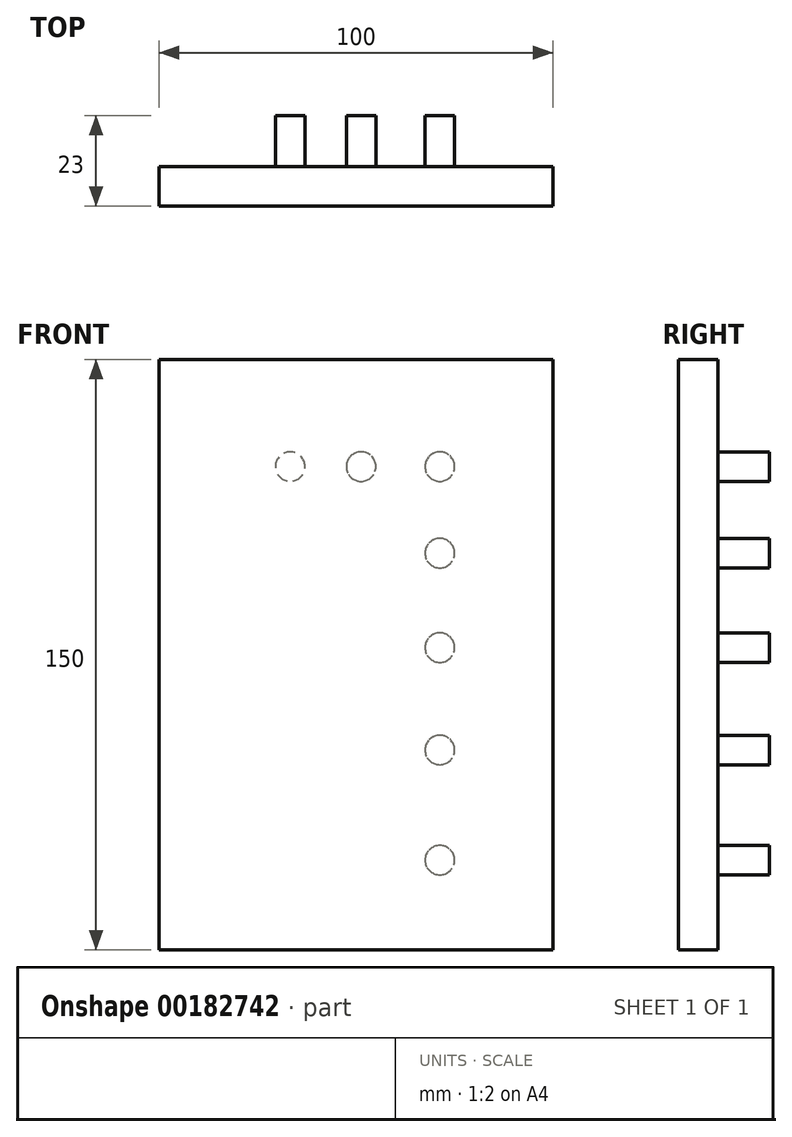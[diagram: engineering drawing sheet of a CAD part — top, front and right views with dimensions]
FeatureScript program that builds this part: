
annotation { "Feature Type Name" : "Feature", "Feature Type Description" : "" }
export const myFeature = defineFeature(function(context is Context, id is Id, definition is map)
    precondition{}
    {
        {
            var Q0;
            Q0=qCreatedBy(makeId("Front.planeOp"),FACE);
            var sketch = newSketch(context, id + "F0", { "sketchPlane" : qUnion([Q0])});
            skLineSegment(sketch, "E0.bottom", {"start": v(-46.92, 108.03) * mm, "end": v(53.08, 108.03) * mm});
            skLineSegment(sketch, "E0.top", {"start": v(-46.92, -41.97) * mm, "end": v(53.08, -41.97) * mm});
            skLineSegment(sketch, "E0.left", {"start": v(-46.92, 108.03) * mm, "end": v(-46.92, -41.97) * mm});
            skLineSegment(sketch, "E0.right", {"start": v(53.08, 108.03) * mm, "end": v(53.08, -41.97) * mm});
            skSolve(sketch);
        }
        {
            var Q0;
            Q0=makeQuery(id+"F0.imprint","IMPRINT",FACE,{"disambiguationData":[TD([[makeQuery(id+"F0.imprint","IMPRINT",EDGE,{"derivedFrom":sQuery(id+"F0.wireOp",EDGE,"E0.bottom")}),-1.0]])]});
            var Q1;
            Q1 = qSketchRegion(id + "FP9mmCFv8DciCVo_1", true);
            var Q2;
            Q2=sQuery(id+"F0.wireOp",EDGE,"E0.right");
            var Q3;
            Q3=sQuery(id+"F0.wireOp",EDGE,"E0.bottom");
            var Q4;
            Q4=sQuery(id+"F0.wireOp",EDGE,"E0.top");
            var Q5;
            Q5=sQuery(id+"F0.wireOp",EDGE,"E0.left");
            extrude(context, id + "F1", {"entities" : qUnion([Q0, Q1]), "surfaceEntities" : qUnion([Q2, Q3, Q4, Q5]), "depth" : 10 * mm});
        }
        {
            var Q0;
            Q0=makeQuery(id+"F1.opExtrude","CAP_FACE",FACE,{"disambiguationData":[OSD([sQuery(id+"F0.wireOp",EDGE,"E0.bottom"),sQuery(id+"F0.wireOp",EDGE,"E0.top"),sQuery(id+"F0.wireOp",EDGE,"E0.left"),sQuery(id+"F0.wireOp",EDGE,"E0.right")])],"isStart":true});
            var sketch = newSketch(context, id + "F2", { "sketchPlane" : qUnion([Q0])});
            skCircle(sketch, "E1", {"center": v(13.61, 80.84) * mm, "radius": 3.75 * mm});
            skCircle(sketch, "E2", {"center": v(-4.39, 80.84) * mm, "radius": 3.75 * mm});
            skCircle(sketch, "E3", {"center": v(-24.39, 80.84) * mm, "radius": 3.75 * mm});
            skCircle(sketch, "E4", {"center": v(-24.39, 58.84) * mm, "radius": 3.75 * mm});
            skCircle(sketch, "E5", {"center": v(-24.39, 34.84) * mm, "radius": 3.75 * mm});
            skCircle(sketch, "E6", {"center": v(-24.39, 8.84) * mm, "radius": 3.75 * mm});
            skCircle(sketch, "E7", {"center": v(-24.39, -19.16) * mm, "radius": 3.75 * mm});
            skSolve(sketch);
        }
        {
            var Q0;
            Q0 = qSketchRegion(id + "F2", true);
            extrude(context, id + "F3", {"entities" : qUnion([Q0]), "operationType" : NewBodyOperationType.ADD, "depth" : 13 * mm});
        }
    });
